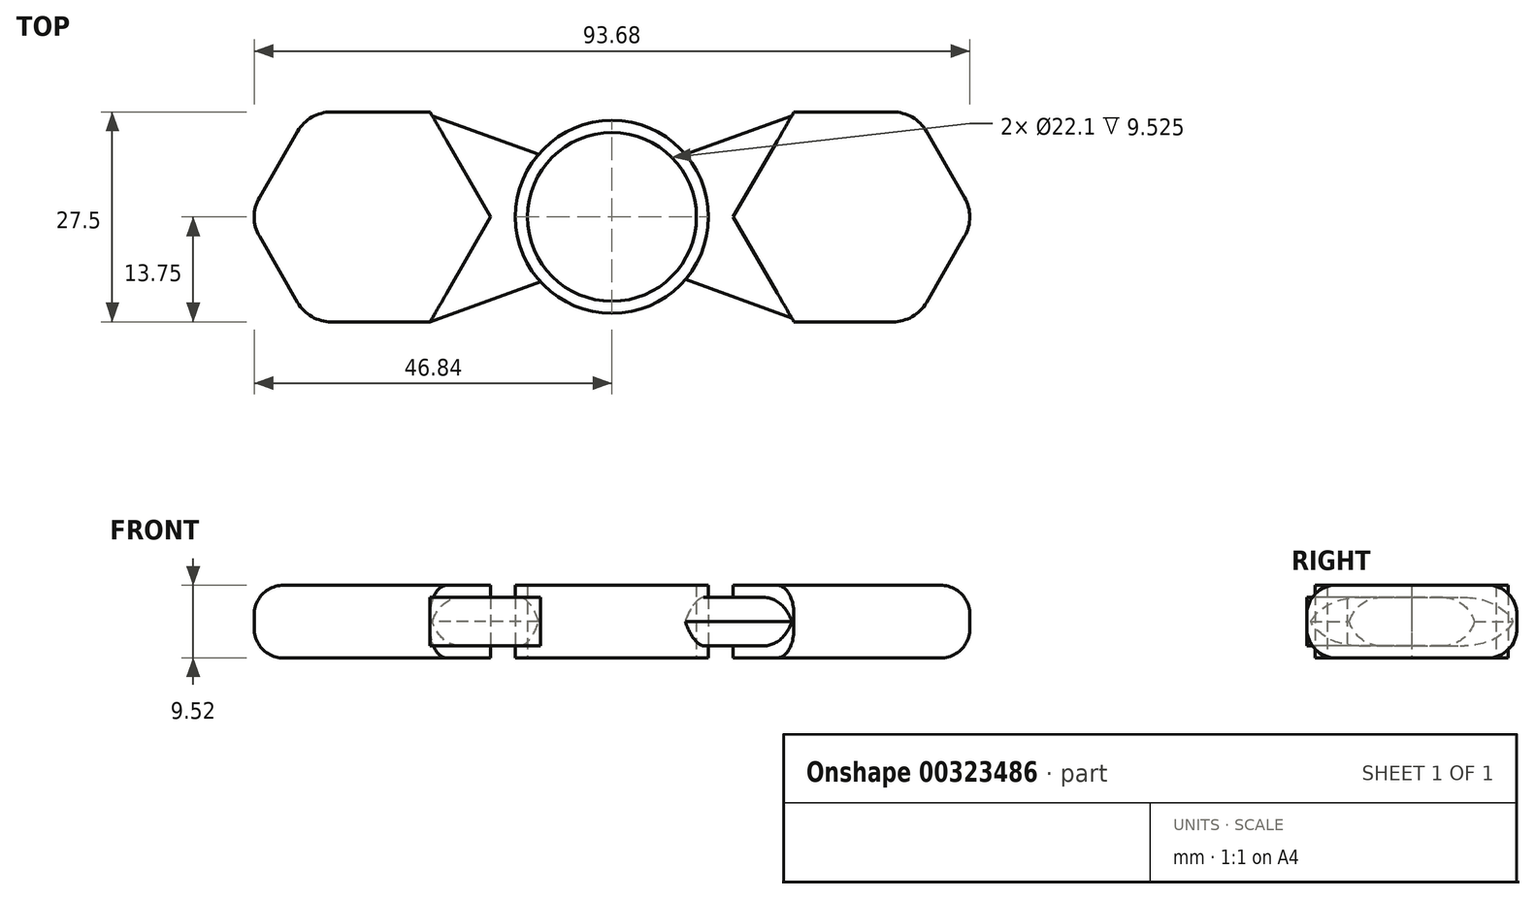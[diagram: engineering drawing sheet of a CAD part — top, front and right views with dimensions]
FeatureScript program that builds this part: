
annotation { "Feature Type Name" : "Feature", "Feature Type Description" : "" }
export const myFeature = defineFeature(function(context is Context, id is Id, definition is map)
    precondition{}
    {
        {
            var Q0;
            Q0=qCreatedBy(makeId("Top.planeOp"),FACE);
            var sketch = newSketch(context, id + "F0", { "sketchPlane" : qUnion([Q0])});
            skCircle(sketch, "E0", {"center": v(0, 0) * mm, "radius": 12.64 * mm});
            skCircle(sketch, "E1", {"center": v(0, 0) * mm, "radius": 11.05 * mm});
            skCircle(sketch, "E2.cCircle", {"center": v(-31.75, 0) * mm, "radius": 15.88 * mm, "construction": true});
            skLineSegment(sketch, "E2.0", {"start": v(-15.87, 0) * mm, "end": v(-23.81, -13.75) * mm});
            skLineSegment(sketch, "E2.1", {"start": v(-23.81, -13.75) * mm, "end": v(-39.69, -13.75) * mm});
            skLineSegment(sketch, "E2.2", {"start": v(-39.69, -13.75) * mm, "end": v(-47.63, 0) * mm});
            skLineSegment(sketch, "E2.3", {"start": v(-47.62, 0) * mm, "end": v(-39.69, 13.75) * mm});
            skLineSegment(sketch, "E2.4", {"start": v(-39.69, 13.75) * mm, "end": v(-23.81, 13.75) * mm});
            skLineSegment(sketch, "E2.5", {"start": v(-23.81, 13.75) * mm, "end": v(-15.87, 0) * mm});
            skCircle(sketch, "E3.cCircle", {"center": v(31.75, 0) * mm, "radius": 15.88 * mm, "construction": true});
            skLineSegment(sketch, "E3.0", {"start": v(15.87, 0) * mm, "end": v(23.81, 13.75) * mm});
            skLineSegment(sketch, "E3.1", {"start": v(23.81, 13.75) * mm, "end": v(39.69, 13.75) * mm});
            skLineSegment(sketch, "E3.2", {"start": v(39.69, 13.75) * mm, "end": v(47.63, 0) * mm});
            skLineSegment(sketch, "E3.3", {"start": v(47.62, 0) * mm, "end": v(39.69, -13.75) * mm});
            skLineSegment(sketch, "E3.4", {"start": v(39.69, -13.75) * mm, "end": v(23.81, -13.75) * mm});
            skLineSegment(sketch, "E3.5", {"start": v(23.81, -13.75) * mm, "end": v(15.87, 0) * mm});
            skLineSegment(sketch, "E4", {"start": v(-31.75, 0) * mm, "end": v(0, 0) * mm, "construction": true});
            skLineSegment(sketch, "E5", {"start": v(0, 0) * mm, "end": v(31.75, 0) * mm, "construction": true});
            skLineSegment(sketch, "E6", {"start": v(-23.81, 13.75) * mm, "end": v(-9.36, 8.49) * mm});
            skLineSegment(sketch, "E7", {"start": v(9.36, 8.49) * mm, "end": v(23.81, 13.75) * mm});
            skLineSegment(sketch, "E8", {"start": v(23.81, -13.75) * mm, "end": v(9.36, -8.49) * mm});
            skLineSegment(sketch, "E9", {"start": v(-9.36, -8.49) * mm, "end": v(-23.81, -13.75) * mm});
            skSolve(sketch);
        }
        {
            var Q0;
            Q0=makeQuery(id+"F0.imprint","IMPRINT",FACE,{"disambiguationData":[TD([[makeQuery(id+"F0.imprint","IMPRINT",EDGE,{"derivedFrom":sQuery(id+"F0.wireOp",EDGE,"E2.0")}),-1.0]])]});
            var Q1;
            Q1=makeQuery(id+"F0.imprint","IMPRINT",FACE,{"disambiguationData":[TD([[makeQuery(id+"F0.imprint","IMPRINT",EDGE,{"derivedFrom":sQuery(id+"F0.wireOp",EDGE,"E1")}),-1.0]])]});
            var Q2;
            Q2=makeQuery(id+"F0.imprint","IMPRINT",FACE,{"disambiguationData":[TD([[makeQuery(id+"F0.imprint","IMPRINT",EDGE,{"derivedFrom":sQuery(id+"F0.wireOp",EDGE,"E3.0")}),-1.0]])]});
            extrude(context, id + "F1", {"entities" : qUnion([Q0, Q1, Q2]), "endBound" : BoundingType.SYMMETRIC, "depth" : 9.52 * mm});
        }
        {
            var Q0;
            Q0=makeQuery(id+"F0.imprint","IMPRINT",FACE,{"disambiguationData":[TD([[makeQuery(id+"F0.imprint","IMPRINT",EDGE,{"derivedFrom":sQuery(id+"F0.wireOp",EDGE,"E2.0")}),1.0]])]});
            var Q1;
            Q1=makeQuery(id+"F0.imprint","IMPRINT",FACE,{"disambiguationData":[TD([[makeQuery(id+"F0.imprint","IMPRINT",EDGE,{"derivedFrom":sQuery(id+"F0.wireOp",EDGE,"E3.0")}),1.0]])]});
            extrude(context, id + "F2", {"entities" : qUnion([Q0, Q1]), "endBound" : BoundingType.SYMMETRIC, "depth" : 6.35 * mm});
        }
        {
            var Q0;
            Q0=makeQuery(id+"F2.opExtrude","CAP_EDGE",EDGE,{"disambiguationData":[OSD([sQuery(id+"F0.wireOp",EDGE,"E2.5")])],"isStart":false});
            var Q1;
            Q1=makeQuery(id+"F2.opExtrude","CAP_EDGE",EDGE,{"disambiguationData":[OSD([sQuery(id+"F0.wireOp",EDGE,"E2.0")])],"isStart":false});
            var Q2;
            Q2=makeQuery(id+"F2.opExtrude","CAP_EDGE",EDGE,{"disambiguationData":[OSD([sQuery(id+"F0.wireOp",EDGE,"E2.0")])],"isStart":true});
            var Q3;
            Q3=makeQuery(id+"F2.opExtrude","CAP_EDGE",EDGE,{"disambiguationData":[OSD([sQuery(id+"F0.wireOp",EDGE,"E2.5")])],"isStart":true});
            var Q4;
            Q4=makeQuery(id+"F2.opExtrude","CAP_EDGE",EDGE,{"disambiguationData":[OSD([sQuery(id+"F0.wireOp",EDGE,"E3.0")])],"isStart":true});
            var Q5;
            Q5=makeQuery(id+"F2.opExtrude","CAP_EDGE",EDGE,{"disambiguationData":[OSD([sQuery(id+"F0.wireOp",EDGE,"E3.5")])],"isStart":true});
            var Q6;
            Q6=makeQuery(id+"F2.opExtrude","CAP_EDGE",EDGE,{"disambiguationData":[OSD([sQuery(id+"F0.wireOp",EDGE,"E3.0")])],"isStart":false});
            var Q7;
            Q7=makeQuery(id+"F2.opExtrude","CAP_EDGE",EDGE,{"disambiguationData":[OSD([sQuery(id+"F0.wireOp",EDGE,"E3.5")])],"isStart":false});
            var Q8;
            {var subQ0=sQuery(id+"F0.wireOp",EDGE,"E0");Q8=makeQuery(id+"F2.opExtrude","CAP_EDGE",EDGE,{"disambiguationData":[OSD([subQ0]),TDD([makeQuery(id+"F0.imprint","IMPRINT",EDGE,{"disambiguationData":[TD([[makeQuery(id+"F0.imprint","INTERSECT",VERTEX,{"derivedFrom":[subQ0,sQuery(id+"F0.wireOp",EDGE,"E6")]}),-1.0]])],"derivedFrom":subQ0})])],"isStart":true});}
            var Q9;
            {var subQ0=sQuery(id+"F0.wireOp",EDGE,"E0");Q9=makeQuery(id+"F2.opExtrude","CAP_EDGE",EDGE,{"disambiguationData":[OSD([subQ0]),TDD([makeQuery(id+"F0.imprint","IMPRINT",EDGE,{"disambiguationData":[TD([[makeQuery(id+"F0.imprint","INTERSECT",VERTEX,{"derivedFrom":[subQ0,sQuery(id+"F0.wireOp",EDGE,"E7")]}),1.0]])],"derivedFrom":subQ0})])],"isStart":true});}
            var Q10;
            {var subQ0=sQuery(id+"F0.wireOp",EDGE,"E0");Q10=makeQuery(id+"F2.opExtrude","CAP_EDGE",EDGE,{"disambiguationData":[OSD([subQ0]),TDD([makeQuery(id+"F0.imprint","IMPRINT",EDGE,{"disambiguationData":[TD([[makeQuery(id+"F0.imprint","INTERSECT",VERTEX,{"derivedFrom":[subQ0,sQuery(id+"F0.wireOp",EDGE,"E7")]}),1.0]])],"derivedFrom":subQ0})])],"isStart":false});}
            var Q11;
            {var subQ0=sQuery(id+"F0.wireOp",EDGE,"E0");Q11=makeQuery(id+"F2.opExtrude","CAP_EDGE",EDGE,{"disambiguationData":[OSD([subQ0]),TDD([makeQuery(id+"F0.imprint","IMPRINT",EDGE,{"disambiguationData":[TD([[makeQuery(id+"F0.imprint","INTERSECT",VERTEX,{"derivedFrom":[subQ0,sQuery(id+"F0.wireOp",EDGE,"E6")]}),-1.0]])],"derivedFrom":subQ0})])],"isStart":false});}
            var Q12;
            Q12=makeQuery(id+"F2.opExtrude","SWEPT_EDGE",EDGE,{"disambiguationData":[OSD([sQuery(id+"F0.wireOp",EDGE,"E0"),sQuery(id+"F0.wireOp",EDGE,"E8")])]});
            var Q13;
            Q13=makeQuery(id+"F2.opExtrude","SWEPT_EDGE",EDGE,{"disambiguationData":[OSD([sQuery(id+"F0.wireOp",EDGE,"E0"),sQuery(id+"F0.wireOp",EDGE,"E9")])]});
            var Q14;
            Q14=makeQuery(id+"F2.opExtrude","SWEPT_EDGE",EDGE,{"disambiguationData":[OSD([sQuery(id+"F0.wireOp",EDGE,"E0"),sQuery(id+"F0.wireOp",EDGE,"E6")])]});
            var Q15;
            Q15=makeQuery(id+"F2.opExtrude","SWEPT_EDGE",EDGE,{"disambiguationData":[OSD([sQuery(id+"F0.wireOp",EDGE,"E0"),sQuery(id+"F0.wireOp",EDGE,"E7")])]});
            var Q16;
            Q16=makeQuery(id+"F1.opExtrude","SWEPT_EDGE",EDGE,{"disambiguationData":[OSD([sQuery(id+"F0.wireOp",EDGE,"E3.3"),sQuery(id+"F0.wireOp",EDGE,"E3.4")])]});
            var Q17;
            Q17=makeQuery(id+"F1.opExtrude","SWEPT_EDGE",EDGE,{"disambiguationData":[OSD([sQuery(id+"F0.wireOp",EDGE,"E3.2"),sQuery(id+"F0.wireOp",EDGE,"E3.3")])]});
            var Q18;
            Q18=makeQuery(id+"F1.opExtrude","SWEPT_EDGE",EDGE,{"disambiguationData":[OSD([sQuery(id+"F0.wireOp",EDGE,"E3.1"),sQuery(id+"F0.wireOp",EDGE,"E3.2")])]});
            var Q19;
            Q19=makeQuery(id+"F1.opExtrude","SWEPT_EDGE",EDGE,{"disambiguationData":[OSD([sQuery(id+"F0.wireOp",EDGE,"E2.3"),sQuery(id+"F0.wireOp",EDGE,"E2.4")])]});
            var Q20;
            Q20=makeQuery(id+"F1.opExtrude","SWEPT_EDGE",EDGE,{"disambiguationData":[OSD([sQuery(id+"F0.wireOp",EDGE,"E2.2"),sQuery(id+"F0.wireOp",EDGE,"E2.3")])]});
            var Q21;
            Q21=makeQuery(id+"F1.opExtrude","SWEPT_EDGE",EDGE,{"disambiguationData":[OSD([sQuery(id+"F0.wireOp",EDGE,"E2.1"),sQuery(id+"F0.wireOp",EDGE,"E2.2")])]});
            fillet(context, id + "F3", {"entities" : qUnion([Q0, Q1, Q2, Q3, Q4, Q5, Q6, Q7, Q8, Q9, Q10, Q11, Q12, Q13, Q14, Q15, Q16, Q17, Q18, Q19, Q20, Q21]), "radius" : 5.08 * mm, "tangentPropagation" : true, "allowEdgeOverflow" : false});
        }
        {
            var Q0;
            Q0=makeQuery(id+"F3.opFillet","BLEND_EDGE",EDGE,{"blendedFrom":[makeQuery(id+"F2.opExtrude","CAP_EDGE",EDGE,{"disambiguationData":[OSD([sQuery(id+"F0.wireOp",EDGE,"E2.0")])],"isStart":false}),makeQuery(id+"F2.opExtrude","SWEPT_FACE",FACE,{"disambiguationData":[OSD([sQuery(id+"F0.wireOp",EDGE,"E9")])]})],"blendedInto":[makeQuery(id+"F2.opExtrude","SWEPT_FACE",FACE,{"disambiguationData":[OSD([sQuery(id+"F0.wireOp",EDGE,"E9")])]})]});
            var Q1;
            Q1=makeQuery(id+"F3.opFillet","BLEND_EDGE",EDGE,{"blendedFrom":[makeQuery(id+"F2.opExtrude","CAP_EDGE",EDGE,{"disambiguationData":[OSD([sQuery(id+"F0.wireOp",EDGE,"E2.0")])],"isStart":true}),makeQuery(id+"F2.opExtrude","SWEPT_FACE",FACE,{"disambiguationData":[OSD([sQuery(id+"F0.wireOp",EDGE,"E9")])]})],"blendedInto":[makeQuery(id+"F2.opExtrude","SWEPT_FACE",FACE,{"disambiguationData":[OSD([sQuery(id+"F0.wireOp",EDGE,"E9")])]})]});
            var Q2;
            Q2=makeQuery(id+"F2.opExtrude","CAP_EDGE",EDGE,{"disambiguationData":[OSD([sQuery(id+"F0.wireOp",EDGE,"E7")])],"isStart":false});
            var Q3;
            Q3=makeQuery(id+"F2.opExtrude","CAP_EDGE",EDGE,{"disambiguationData":[OSD([sQuery(id+"F0.wireOp",EDGE,"E8")])],"isStart":false});
            var Q4;
            Q4=makeQuery(id+"F2.opExtrude","CAP_EDGE",EDGE,{"disambiguationData":[OSD([sQuery(id+"F0.wireOp",EDGE,"E7")])],"isStart":true});
            var Q5;
            Q5=makeQuery(id+"F2.opExtrude","CAP_EDGE",EDGE,{"disambiguationData":[OSD([sQuery(id+"F0.wireOp",EDGE,"E8")])],"isStart":true});
            var Q6;
            Q6=makeQuery(id+"F2.opExtrude","CAP_EDGE",EDGE,{"disambiguationData":[OSD([sQuery(id+"F0.wireOp",EDGE,"E6")])],"isStart":true});
            var Q7;
            Q7=makeQuery(id+"F2.opExtrude","CAP_EDGE",EDGE,{"disambiguationData":[OSD([sQuery(id+"F0.wireOp",EDGE,"E6")])],"isStart":false});
            fillet(context, id + "F4", {"entities" : qUnion([Q0, Q1, Q2, Q3, Q4, Q5, Q6, Q7]), "radius" : 5.08 * mm, "tangentPropagation" : true, "allowEdgeOverflow" : false});
        }
        {
            var Q0;
            Q0=makeQuery(id+"F1.opExtrude","CAP_EDGE",EDGE,{"disambiguationData":[OSD([sQuery(id+"F0.wireOp",EDGE,"E2.4")])],"isStart":false});
            var Q1;
            Q1=makeQuery(id+"F1.opExtrude","CAP_EDGE",EDGE,{"disambiguationData":[OSD([sQuery(id+"F0.wireOp",EDGE,"E3.1")])],"isStart":false});
            var Q2;
            Q2=makeQuery(id+"F1.opExtrude","CAP_EDGE",EDGE,{"disambiguationData":[OSD([sQuery(id+"F0.wireOp",EDGE,"E2.4")])],"isStart":true});
            var Q3;
            Q3=makeQuery(id+"F1.opExtrude","CAP_EDGE",EDGE,{"disambiguationData":[OSD([sQuery(id+"F0.wireOp",EDGE,"E3.1")])],"isStart":true});
            fillet(context, id + "F5", {"entities" : qUnion([Q0, Q1, Q2, Q3]), "radius" : 3.8 * mm, "tangentPropagation" : true, "allowEdgeOverflow" : false});
        }
    });
